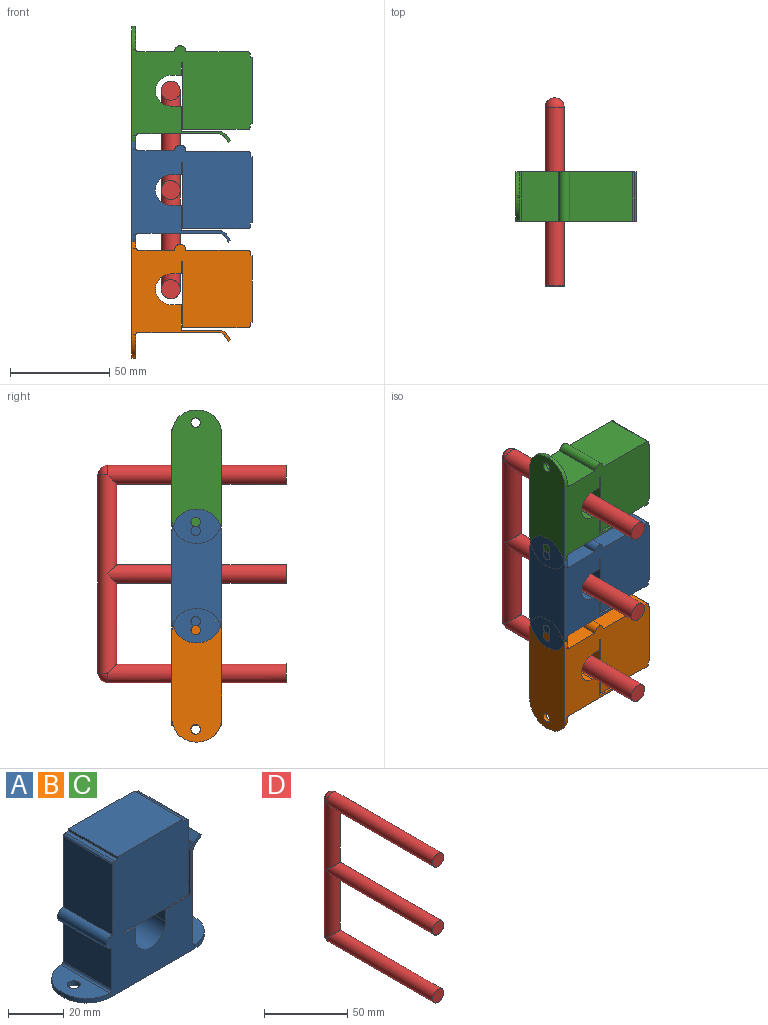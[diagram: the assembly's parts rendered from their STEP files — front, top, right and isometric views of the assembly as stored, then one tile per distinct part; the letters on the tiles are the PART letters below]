
ASSEMBLY  parts=4 mates=7
PART A: 44 faces, bbox 67.2x25x60.5 mm
  f0: plane 25x1.94mm, normal (-0.87,0,0.5), area 55.9mm2, adj f1,f35,f36,f37
  f1: cylinder r=1mm len=25mm, axis (0,1,0), area 13.1mm2, adj f0,f2,f36,f37
  f2: plane 25x19.83mm, normal (-1,0,0), area 495.7mm2, adj f1,f3,f36,f37
  f3: plane 25x12.86mm, normal (0,0,1), area 321.5mm2, adj f2,f4,f36,f37
  f4: plane 25x5.28mm, normal (-1,0,0), area 132.1mm2, adj f3,f5,f36,f37
  f5: cylinder r=7.71mm len=25mm, axis (0,1,0), area 606.1mm2, adj f4,f6,f36,f37
  f6: plane 25x5.3mm, normal (1,0,0), area 132.4mm2, adj f5,f7,f36,f37
  f7: plane 25x6.36mm, normal (0,0,1), area 159.1mm2, adj f6,f8,f36,f37
  f8: plane 25x0.56mm, normal (1,0,0), area 14.1mm2, adj f7,f9,f36,f37
  f9: plane 33.49x25mm, normal (0,0,-1), area 837.3mm2, adj f8,f10,f36,f37
  f10: plane 33.09x25mm, normal (1,0,0), area 827.2mm2, adj f9,f11,f36,f37
  f11: cylinder r=1mm len=25mm, axis (0,1,0), area 39.3mm2, adj f10,f12,f36,f37
  f12: plane 25x1.79mm, normal (0,0,1), area 44.7mm2, adj f11,f13,f36,f37
  f13: plane 25x0.98mm, normal (1,0,0), area 24.6mm2, adj f12,f14,f36,f37
  f14: plane 33.47x25mm, normal (0,0,1), area 836.6mm2, adj f13,f15,f36,f37
  f15: plane 25x0.98mm, normal (-1,0,0), area 24.6mm2, adj f14,f16,f36,f37
  f16: plane 25x1.74mm, normal (0,0,1), area 43.4mm2, adj f15,f17,f36,f37
  f17: cylinder r=1mm len=25mm, axis (0,1,0), area 39.3mm2, adj f16,f18,f36,f37
  f18: plane 31.35x25mm, normal (-1,0,0), area 783.7mm2, adj f17,f19,f36,f37
  f19: cylinder r=2.87mm len=25mm, axis (0,1,0), area 229.6mm2, adj f18,f20,f36,f37
  f20: plane 25x18.43mm, normal (-1,0,0), area 460.8mm2, adj f19,f21,f36,f37
  f21: cylinder r=1mm len=25mm, axis (0,1,0), area 39.3mm2, adj f20,f22,f36,f37,f39,f41
  f22: plane 25x11.86mm, normal (0,0,1), area 217.1mm2, adj f21,f23,f39,f41,f43
  f23: plane 1.99x1.06mm, normal (-1,0,0), area 2.1mm2, adj f22,f24,f39,f41
  f24: plane 67.19x25mm, normal (0,0,-1), area 1521.2mm2, adj f23,f25,f36,f37,f38,f39,f40,f41
  f25: plane 1.99x1.06mm, normal (1,0,0), area 2.1mm2, adj f24,f26,f38,f40
  f26: plane 25x11.82mm, normal (0,0,1), area 216.1mm2, adj f25,f27,f38,f40,f42
  f27: cylinder r=1mm len=25mm, axis (0,1,0), area 39.3mm2, adj f26,f28,f36,f37,f38,f40
  f28: plane 41.16x25mm, normal (1,0,0), area 1029mm2, adj f27,f29,f36,f37
  f29: cylinder r=1mm len=25mm, axis (0,1,0), area 13.1mm2, adj f28,f30,f36,f37
  f30: plane 25x1.5mm, normal (0.87,0,-0.5), area 43.3mm2, adj f29,f31,f36,f37
  f31: cylinder r=1mm len=25mm, axis (0,1,0), area 10.8mm2, adj f30,f32,f36,f37
  f32: plane 25x3.2mm, normal (0.58,0,-0.82), area 97.8mm2, adj f31,f33,f36,f37
  f33: plane 25x0.98mm, normal (0.71,0,0.7), area 34.3mm2, adj f32,f34,f36,f37
  f34: plane 25x3.21mm, normal (-0.58,0,0.82), area 98.1mm2, adj f33,f35,f36,f37
  f35: cylinder r=1mm len=25mm, axis (0,1,0), area 10.8mm2, adj f0,f34,f36,f37
  f36: plane 60.49x48.89mm, normal (0,-1,0), area 2271.9mm2, adj f0,f1,f2,f3,f4,f5,f6,f7
  f37: plane 60.49x48.89mm, normal (0,1,0), area 2271.9mm2, adj f0,f1,f2,f3,f4,f5,f6,f7
  f38: cylinder r=11.97mm len=11.97mm, axis (0,0,1), area 37.4mm2, adj f24,f25,f26,f27,f37
  f39: cylinder r=11.97mm len=11.97mm, axis (0,0,-1), area 37.4mm2, adj f21,f22,f23,f24,f37
  f40: cylinder r=11.97mm len=11.97mm, axis (0,0,-1), area 37.4mm2, adj f24,f25,f26,f27,f36
  f41: cylinder r=11.97mm len=11.97mm, axis (0,0,1), area 37.4mm2, adj f21,f22,f23,f24,f36
  f42: cylinder r=2.38mm len=4.76mm, axis (0,0,-1), area 29.8mm2, adj f24,f26
  f43: cylinder r=2.38mm len=4.76mm, axis (0,0,-1), area 29.8mm2, adj f22,f24
PART B: same geometry as A
PART C: same geometry as A
PART D: 9 faces, bbox 9.5x94.8x109.5 mm
  f0: cylinder r=4.76mm len=90mm, axis (0,1,0), area 2647.8mm2, adj f1,f2,f3
  f1: plane 9.53x9.53mm, normal (0,-1,0), area 71.3mm2, adj f0
  f2: cylinder r=4.76mm len=100mm, axis (0,0,1), area 2810.9mm2, adj f0,f3,f4,f6,f7
  f3: sphere r=4.76mm, area 71.3mm2, adj f0,f2
  f4: cylinder r=4.76mm len=90mm, axis (0,1,0), area 2647.8mm2, adj f2,f5,f6
  f5: plane 9.53x9.53mm, normal (0,-1,0), area 71.3mm2, adj f4
  f6: sphere r=4.76mm, area 71.3mm2, adj f2,f4
  f7: cylinder r=4.76mm len=90mm, axis (0,1,0), area 2602.4mm2, adj f2,f8
  f8: plane 9.53x9.53mm, normal (0,-1,0), area 71.3mm2, adj f7
PLACE A rot(axis=(0,1,0),90deg) t=(-84.71,21.95,79.48)mm
PLACE B rot(axis=(0,1,0),90deg) t=(-84.71,21.95,29.48)mm
PLACE C rot(axis=(0,1,0),90deg) t=(-84.71,21.95,129.48)mm
PLACE D t=(-65.15,54.45,-3.09)mm fixed
MATE cylindrical A.f5 <-> D.f7  axis (0,1,0) through (-65.15,9.45,46.91)mm
MATE cylindrical B.f5 <-> D.f0  axis (0,1,0) through (-65.15,9.45,-3.09)mm
MATE parallel C.f28 <-> B.f28  axis (0,0,-1) through (-61.14,9.45,75.11)mm
MATE parallel B.f28 <-> A.f28  axis (0,0,-1) through (-61.14,9.45,-24.89)mm
MATE cylindrical D.f4 <-> C.f5  axis (0,1,0) through (-65.15,9.45,96.91)mm
MATE planar C.f36 <-> B.f36  axis (0,-1,0) through (-54.1,-3.05,96.31)mm
MATE planar C.f36 <-> A.f36  axis (0,-1,0) through (-54.1,-3.05,96.31)mm
